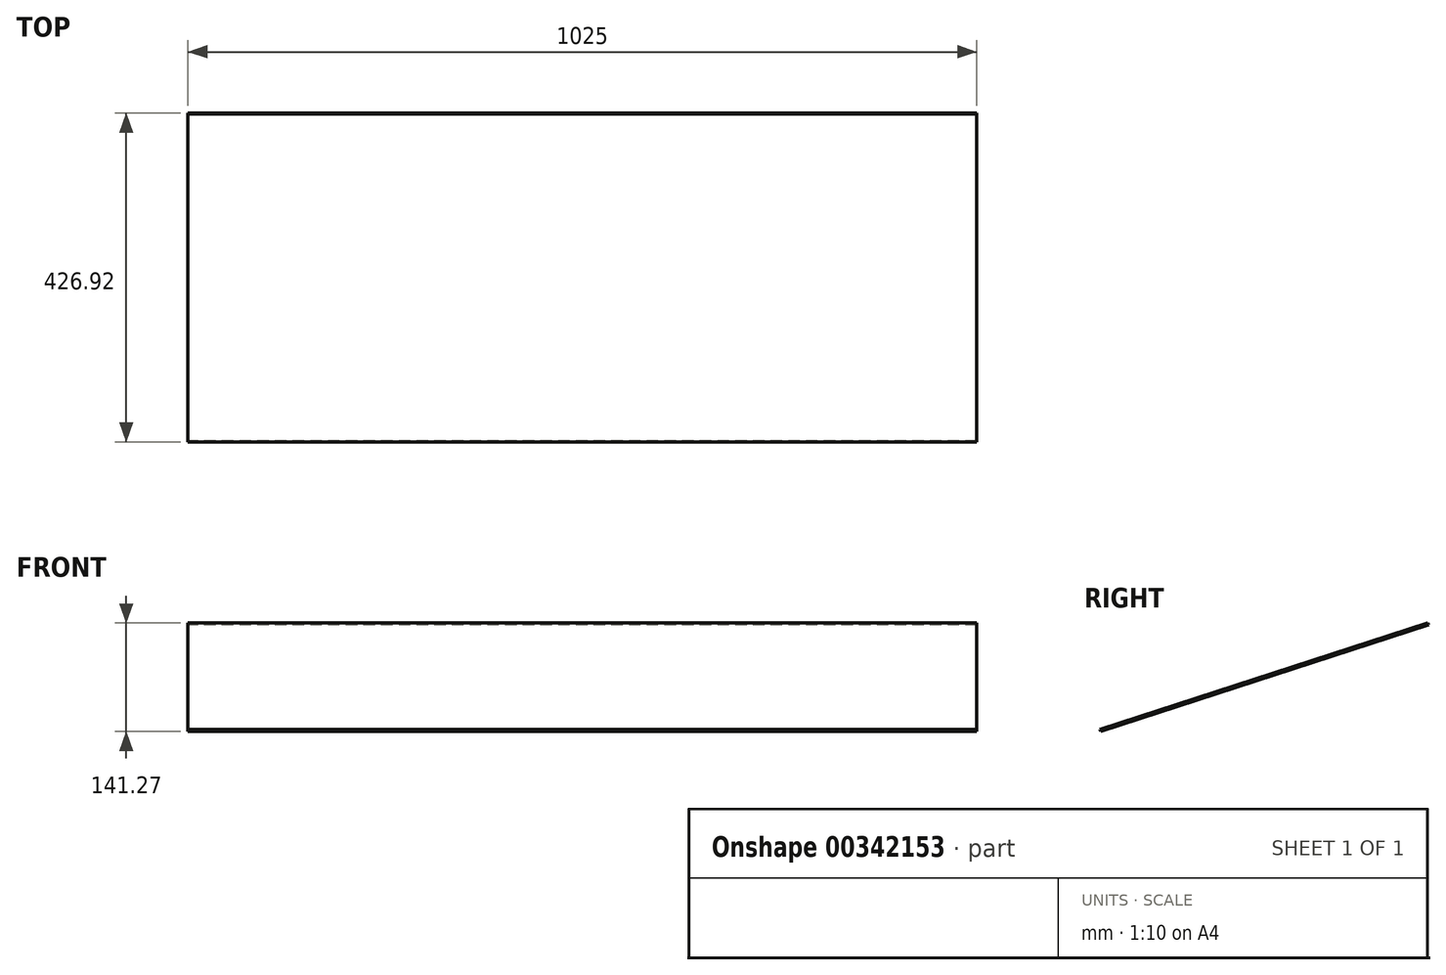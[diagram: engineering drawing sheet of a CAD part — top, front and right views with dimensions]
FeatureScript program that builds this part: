
annotation { "Feature Type Name" : "Feature", "Feature Type Description" : "" }
export const myFeature = defineFeature(function(context is Context, id is Id, definition is map)
    precondition{}
    {
        {
            var Q0;
            Q0=qCreatedBy(makeId("Right.planeOp"),FACE);
            var sketch = newSketch(context, id + "F0", { "sketchPlane" : qUnion([Q0])});
            skLineSegment(sketch, "E0", {"start": v(0, 0) * mm, "end": v(2288, 0) * mm});
            skLineSegment(sketch, "E1", {"start": v(2288, 0) * mm, "end": v(2288, 684.37) * mm});
            skLineSegment(sketch, "E2", {"start": v(2100, 0) * mm, "end": v(2100, 623.29) * mm});
            skLineSegment(sketch, "E3", {"start": v(2050, 0) * mm, "end": v(2050, 607.04) * mm});
            skLineSegment(sketch, "E4", {"start": v(2100, 623.29) * mm, "end": v(2288, 684.37) * mm});
            skLineSegment(sketch, "E5", {"start": v(2100, 623.29) * mm, "end": v(2050, 607.04) * mm});
            skLineSegment(sketch, "E6", {"start": v(2050, 607.04) * mm, "end": v(1862, 545.95) * mm});
            skLineSegment(sketch, "E7", {"start": v(2050, 607.04) * mm, "end": v(2041.35, 633.67) * mm});
            skLineSegment(sketch, "E8", {"start": v(2100, 623.29) * mm, "end": v(2091.35, 649.92) * mm});
            skLineSegment(sketch, "E9", {"start": v(2288, 684.37) * mm, "end": v(2279.35, 711) * mm});
            skLineSegment(sketch, "E10", {"start": v(2279.35, 711) * mm, "end": v(2091.35, 649.92) * mm});
            skLineSegment(sketch, "E11", {"start": v(2091.35, 649.92) * mm, "end": v(2041.35, 633.67) * mm});
            skLineSegment(sketch, "E12", {"start": v(2041.35, 633.67) * mm, "end": v(1853.35, 572.58) * mm});
            skLineSegment(sketch, "E13", {"start": v(1853.35, 572.58) * mm, "end": v(1862, 545.95) * mm});
            skLineSegment(sketch, "E14", {"start": v(1854.27, 569.73) * mm, "end": v(2280.27, 708.15) * mm});
            skSolve(sketch);
        }
        {
            var Q0;
            {var subQ0=sQuery(id+"F0.wireOp",EDGE,"0M8AAAyR-SB0r-MtMV-LE9l-MARlShi8dbRd");Q0=makeQuery(id+"F0.imprint","IMPRINT",FACE,{"disambiguationData":[TD([[makeQuery(id+"F0.imprint","IMPRINT",EDGE,{"derivedFrom":subQ0}),-1.0]])]});}
            var Q1;
            {var subQ0=sQuery(id+"F0.wireOp",EDGE,"1FGk7jgl-vVaA-wB1T-qpKy-0b2ghD9h8zY1");Q1=makeQuery(id+"F0.imprint","IMPRINT",FACE,{"disambiguationData":[TD([[makeQuery(id+"F0.imprint","IMPRINT",EDGE,{"derivedFrom":subQ0}),1.0]])]});}
            var Q2;
            {var subQ0=sQuery(id+"F0.wireOp",EDGE,"ccb0210a-ae8c-467c-bc7f-bc7526da68d5.trimOffspring");Q2=makeQuery(id+"F0.imprint","IMPRINT",FACE,{"disambiguationData":[TD([[makeQuery(id+"F0.imprint","IMPRINT",EDGE,{"derivedFrom":subQ0}),-1.0]])]});}
            var Q3;
            {var subQ0=sQuery(id+"F0.wireOp",EDGE,"E12");Q3=makeQuery(id+"F0.imprint","IMPRINT",FACE,{"disambiguationData":[TD([[makeQuery(id+"F0.imprint","IMPRINT",EDGE,{"derivedFrom":subQ0}),1.0]])]});}
            var Q4;
            {var subQ0=sQuery(id+"F0.wireOp",EDGE,"E11");Q4=makeQuery(id+"F0.imprint","IMPRINT",FACE,{"disambiguationData":[TD([[makeQuery(id+"F0.imprint","IMPRINT",EDGE,{"derivedFrom":subQ0}),1.0]])]});}
            var Q5;
            {var subQ0=sQuery(id+"F0.wireOp",EDGE,"E10");Q5=makeQuery(id+"F0.imprint","IMPRINT",FACE,{"disambiguationData":[TD([[makeQuery(id+"F0.imprint","IMPRINT",EDGE,{"derivedFrom":subQ0}),1.0]])]});}
            extrude(context, id + "F1", {"entities" : qUnion([Q0, Q1, Q2, Q3, Q4, Q5]), "endBound" : BoundingType.SYMMETRIC, "depth" : 1100 * mm});
        }
        {
            var Q0;
            Q0=makeQuery(id+"F1.opExtrude","SWEPT_FACE",FACE,{"disambiguationData":[OSD([sQuery(id+"F0.wireOp",EDGE,"E10"),sQuery(id+"F0.wireOp",EDGE,"E11"),sQuery(id+"F0.wireOp",EDGE,"E12")])]});
            var sketch = newSketch(context, id + "F2", { "sketchPlane" : qUnion([Q0])});
            skLineSegment(sketch, "E15", {"start": v(0, 2163.54) * mm, "end": v(500, 2163.54) * mm});
            skPoint(sketch, "E15.startSnap0", {"position": v(550, 2163.54) * mm});
            skPoint(sketch, "E15.startSnap1", {"position": v(0, 2387.5) * mm});
            skPoint(sketch, "E15.endSnap0", {"position": v(550, 2163.54) * mm});
            skLineSegment(sketch, "E16", {"start": v(500, 2188.54) * mm, "end": v(475, 2188.54) * mm});
            skLineSegment(sketch, "E17", {"start": v(475, 2188.54) * mm, "end": v(475, 2138.54) * mm});
            skLineSegment(sketch, "E18", {"start": v(475, 2138.54) * mm, "end": v(500, 2138.54) * mm});
            skLineSegment(sketch, "E19.bottom", {"start": v(462.5, 2387.5) * mm, "end": v(512.5, 2387.5) * mm});
            skLineSegment(sketch, "E19.top", {"start": v(462.5, 1939.58) * mm, "end": v(512.5, 1939.58) * mm});
            skLineSegment(sketch, "E19.left", {"start": v(462.5, 2387.5) * mm, "end": v(462.5, 1939.58) * mm});
            skLineSegment(sketch, "E19.right", {"start": v(512.5, 2387.5) * mm, "end": v(512.5, 1939.58) * mm});
            skPoint(sketch, "E19.middle", {"position": v(487.5, 2163.54) * mm});
            skPoint(sketch, "E19.middle.positionSnap0", {"position": v(487.5, 2138.54) * mm});
            skPoint(sketch, "E19.centerSnap0", {"position": v(487.5, 2138.54) * mm});
            skLineSegment(sketch, "E20.MirrorCS", {"start": v(0, 2163.54) * mm, "end": v(-500, 2163.54) * mm});
            skLineSegment(sketch, "E21.MirrorCS", {"start": v(-462.5, 2387.5) * mm, "end": v(-462.5, 1939.58) * mm});
            skLineSegment(sketch, "E22.MirrorCS", {"start": v(-475, 2188.54) * mm, "end": v(-475, 2138.54) * mm});
            skLineSegment(sketch, "E23.MirrorCS", {"start": v(-475, 2138.54) * mm, "end": v(-500, 2138.54) * mm});
            skLineSegment(sketch, "E24.MirrorCS", {"start": v(-500, 2138.54) * mm, "end": v(-500, 2163.54) * mm});
            skLineSegment(sketch, "E25.MirrorCS", {"start": v(-500, 2163.54) * mm, "end": v(-500, 2188.54) * mm});
            skLineSegment(sketch, "E26.MirrorCS", {"start": v(-500, 2188.54) * mm, "end": v(-475, 2188.54) * mm});
            skLineSegment(sketch, "E27.MirrorCS", {"start": v(-512.5, 2387.5) * mm, "end": v(-512.5, 1939.58) * mm});
            skLineSegment(sketch, "E28", {"start": v(500, 2138.54) * mm, "end": v(500, 2188.54) * mm});
            skSolve(sketch);
        }
        {
            var Q0;
            {var subQ0=sQuery(id+"F2.wireOp",EDGE,"E27.MirrorCS");Q0=makeQuery(id+"F2.imprint","IMPRINT",FACE,{"disambiguationData":[TD([[makeQuery(id+"F2.imprint","IMPRINT",EDGE,{"derivedFrom":subQ0}),-1.0]])]});}
            var Q1;
            {var subQ0=sQuery(id+"F2.wireOp",EDGE,"E19.right");Q1=makeQuery(id+"F2.imprint","IMPRINT",FACE,{"disambiguationData":[TD([[makeQuery(id+"F2.imprint","IMPRINT",EDGE,{"derivedFrom":subQ0}),1.0]])]});}
            extrude(context, id + "F3", {"entities" : qUnion([Q0, Q1]), "operationType" : NewBodyOperationType.REMOVE, "oppositeDirection" : true, "depth" : 25 * mm});
        }
    });
